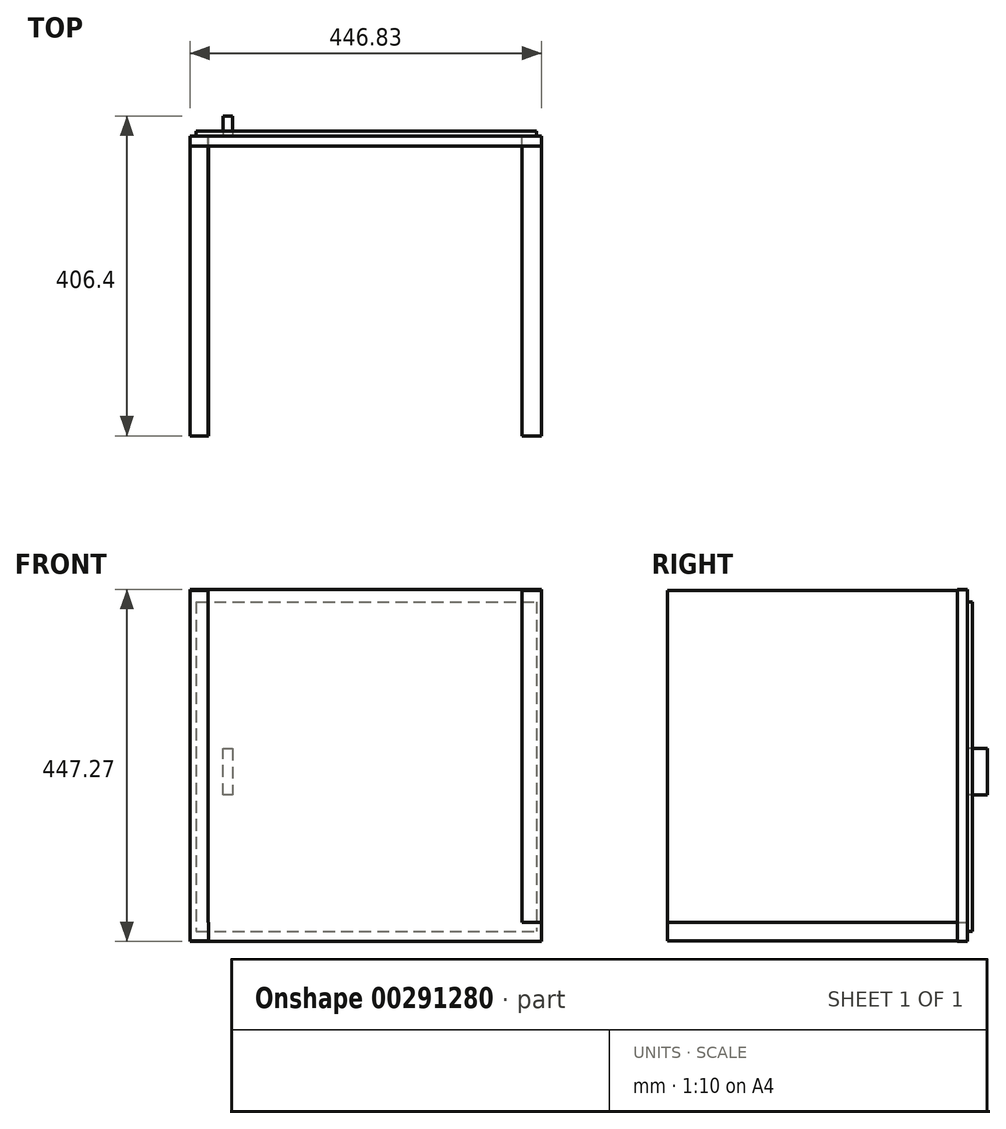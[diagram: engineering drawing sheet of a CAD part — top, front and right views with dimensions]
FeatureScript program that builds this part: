
annotation { "Feature Type Name" : "Feature", "Feature Type Description" : "" }
export const myFeature = defineFeature(function(context is Context, id is Id, definition is map)
    precondition{}
    {
        {
            var Q0;
            Q0=qCreatedBy(makeId("Front.planeOp"),FACE);
            var sketch = newSketch(context, id + "F0", { "sketchPlane" : qUnion([Q0])});
            skLineSegment(sketch, "E0.bottom", {"start": v(199.26, -198.54) * mm, "end": v(-199.26, -198.54) * mm});
            skLineSegment(sketch, "E0.top", {"start": v(199.26, 198.54) * mm, "end": v(-199.26, 198.54) * mm});
            skLineSegment(sketch, "E0.left", {"start": v(199.26, -198.54) * mm, "end": v(199.26, 198.54) * mm});
            skLineSegment(sketch, "E0.right", {"start": v(-199.26, -198.54) * mm, "end": v(-199.26, 198.54) * mm});
            skPoint(sketch, "E0.middle", {"position": v(0, 0) * mm});
            skLineSegment(sketch, "E1.bottom", {"start": v(-199.26, 198.54) * mm, "end": v(199.26, 198.54) * mm});
            skLineSegment(sketch, "E1.top", {"start": v(-199.26, 223.47) * mm, "end": v(199.26, 223.47) * mm});
            skLineSegment(sketch, "E1.left", {"start": v(-199.26, 198.54) * mm, "end": v(-199.26, 223.47) * mm});
            skLineSegment(sketch, "E1.right", {"start": v(199.26, 198.54) * mm, "end": v(199.26, 223.47) * mm});
            skLineSegment(sketch, "E2.bottom", {"start": v(199.26, 223.47) * mm, "end": v(223.65, 223.47) * mm});
            skLineSegment(sketch, "E2.top", {"start": v(199.26, -198.54) * mm, "end": v(223.65, -198.54) * mm});
            skLineSegment(sketch, "E2.left", {"start": v(199.26, 223.47) * mm, "end": v(199.26, -198.54) * mm});
            skLineSegment(sketch, "E2.right", {"start": v(223.65, 223.47) * mm, "end": v(223.65, -198.54) * mm});
            skLineSegment(sketch, "E3.bottom", {"start": v(223.65, -198.54) * mm, "end": v(-199.58, -198.54) * mm});
            skLineSegment(sketch, "E3.top", {"start": v(223.65, -221.72) * mm, "end": v(-199.58, -221.72) * mm});
            skLineSegment(sketch, "E3.left", {"start": v(223.65, -198.54) * mm, "end": v(223.65, -221.72) * mm});
            skLineSegment(sketch, "E3.right", {"start": v(-199.58, -198.54) * mm, "end": v(-199.58, -221.72) * mm});
            skLineSegment(sketch, "E4.left", {"start": v(-199.58, -221.72) * mm, "end": v(-199.58, 223.47) * mm});
            skLineSegment(sketch, "E5.bottom", {"start": v(-199.26, 223.47) * mm, "end": v(-222.75, 223.47) * mm});
            skLineSegment(sketch, "E5.top", {"start": v(-199.26, -221.72) * mm, "end": v(-222.75, -221.72) * mm});
            skLineSegment(sketch, "E5.left", {"start": v(-199.26, 223.47) * mm, "end": v(-199.26, -221.72) * mm});
            skLineSegment(sketch, "E5.right", {"start": v(-222.75, 223.47) * mm, "end": v(-222.75, -221.72) * mm});
            skSolve(sketch);
        }
        {
            var Q0;
            {var subQ3=sQuery(id+"F0.wireOp",EDGE,"E5.right");Q0=makeQuery(id+"F0.imprint","IMPRINT",FACE,{"disambiguationData":[TD([[makeQuery(id+"F0.imprint","IMPRINT",EDGE,{"derivedFrom":subQ3}),1.0]])]});}
            var Q1;
            {var subQ0=sQuery(id+"F0.wireOp",EDGE,"E1.bottom");Q1=makeQuery(id+"F0.imprint","IMPRINT",FACE,{"disambiguationData":[TD([[makeQuery(id+"F0.imprint","IMPRINT",EDGE,{"derivedFrom":subQ0}),1.0]])]});}
            var Q2;
            {var subQ5=sQuery(id+"F0.wireOp",EDGE,"E2.bottom");Q2=makeQuery(id+"F0.imprint","IMPRINT",FACE,{"disambiguationData":[TD([[makeQuery(id+"F0.imprint","IMPRINT",EDGE,{"derivedFrom":subQ5}),-1.0]])]});}
            var Q3;
            {var subQ1=sQuery(id+"F0.wireOp",EDGE,"E3.top");Q3=makeQuery(id+"F0.imprint","IMPRINT",FACE,{"disambiguationData":[TD([[makeQuery(id+"F0.imprint","IMPRINT",EDGE,{"derivedFrom":subQ1}),-1.0]])]});}
            extrude(context, id + "F1", {"entities" : qUnion([Q0, Q1, Q2, Q3]), "depth" : 381 * mm});
        }
        {
            var Q0;
            Q0=qCreatedBy(makeId("Front.planeOp"),FACE);
            var sketch = newSketch(context, id + "F2", { "sketchPlane" : qUnion([Q0])});
            skLineSegment(sketch, "E6.bottom", {"start": v(-222.34, 224.5) * mm, "end": v(224.08, 224.5) * mm});
            skLineSegment(sketch, "E6.top", {"start": v(-222.34, -222.76) * mm, "end": v(224.08, -222.76) * mm});
            skLineSegment(sketch, "E6.left", {"start": v(-222.34, 224.5) * mm, "end": v(-222.34, -222.76) * mm});
            skLineSegment(sketch, "E6.right", {"start": v(224.08, 224.5) * mm, "end": v(224.08, -222.76) * mm});
            skSolve(sketch);
        }
        {
            var Q0;
            Q0 = qSketchRegion(id + "F2", true);
            extrude(context, id + "F3", {"entities" : qUnion([Q0]), "depth" : 12.7 * mm});
        }
        {
            var Q0;
            Q0=qCreatedBy(makeId("Front.planeOp"),FACE);
            var sketch = newSketch(context, id + "F4", { "sketchPlane" : qUnion([Q0])});
            skLineSegment(sketch, "E7.bottom", {"start": v(-214.58, 208.84) * mm, "end": v(217.61, 208.84) * mm});
            skLineSegment(sketch, "E7.top", {"start": v(-214.58, -209.86) * mm, "end": v(217.61, -209.86) * mm});
            skLineSegment(sketch, "E7.left", {"start": v(-214.58, 208.84) * mm, "end": v(-214.58, -209.86) * mm});
            skLineSegment(sketch, "E7.right", {"start": v(217.61, 208.84) * mm, "end": v(217.61, -209.86) * mm});
            skSolve(sketch);
        }
        {
            var Q0;
            Q0 = qSketchRegion(id + "F4", true);
            extrude(context, id + "F5", {"entities" : qUnion([Q0]), "oppositeDirection" : true, "depth" : 6.35 * mm});
        }
        {
            var Q0;
            Q0=qCreatedBy(makeId("Front.planeOp"),FACE);
            var sketch = newSketch(context, id + "F6", { "sketchPlane" : qUnion([Q0])});
            skLineSegment(sketch, "E8", {"start": v(-168.65, 22.22) * mm, "end": v(-168.65, -36.74) * mm});
            skLineSegment(sketch, "E9", {"start": v(-168.65, -36.74) * mm, "end": v(-180.85, -36.74) * mm});
            skLineSegment(sketch, "E10", {"start": v(-180.85, -36.74) * mm, "end": v(-180.85, 22.22) * mm});
            skLineSegment(sketch, "E11", {"start": v(-180.85, 22.22) * mm, "end": v(-168.65, 22.22) * mm});
            skSolve(sketch);
        }
        {
            var Q0;
            Q0 = qSketchRegion(id + "F6", true);
            extrude(context, id + "F7", {"entities" : qUnion([Q0]), "oppositeDirection" : true, "depth" : 25.4 * mm});
        }
    });
